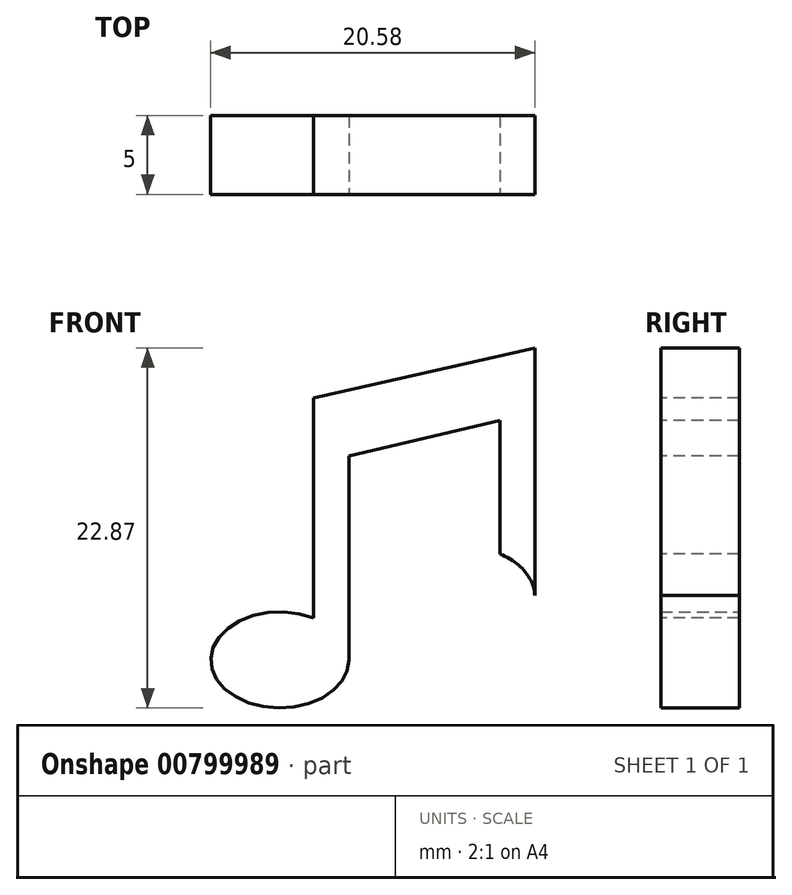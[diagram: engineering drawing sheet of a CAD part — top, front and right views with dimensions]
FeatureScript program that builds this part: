
annotation { "Feature Type Name" : "Feature", "Feature Type Description" : "" }
export const myFeature = defineFeature(function(context is Context, id is Id, definition is map)
    precondition{}
    {
        {
            var Q0;
            Q0=qCreatedBy(makeId("Front.planeOp"),FACE);
            var sketch = newSketch(context, id + "F0", { "sketchPlane" : qUnion([Q0])});
            skLineSegment(sketch, "E0", {"start": v(-6.22, 7.22) * mm, "end": v(7.82, 10.4) * mm});
            skLineSegment(sketch, "E1", {"start": v(7.82, 10.4) * mm, "end": v(7.82, -5.52) * mm});
            skLineSegment(sketch, "E2", {"start": v(-6.22, 7.22) * mm, "end": v(-6.22, -6.76) * mm});
            skLineSegment(sketch, "E3", {"start": v(-3.98, -9.42) * mm, "end": v(-3.98, 3.54) * mm});
            skLineSegment(sketch, "E4", {"start": v(-3.98, 3.54) * mm, "end": v(5.6, 5.78) * mm});
            skLineSegment(sketch, "E5", {"start": v(5.6, 5.78) * mm, "end": v(5.6, -2.69) * mm});
            skEllipse(sketch, "E6", {"center": v(-8.37, -9.42) * mm, "majorRadius": 4.39 * mm, "minorRadius": 3.05 * mm, "majorAxis": v(1, 0)});
            skEllipse(sketch, "E7", {"center": v(3.53, -5.32) * mm, "majorRadius": 4.3 * mm, "minorRadius": 3.06 * mm, "majorAxis": v(1, -0.05)});
            skSolve(sketch);
        }
        {
            var Q0;
            {var subQ3=sQuery(id+"F0.wireOp",EDGE,"E0");Q0=makeQuery(id+"F0.imprint","IMPRINT",FACE,{"disambiguationData":[TD([[makeQuery(id+"F0.imprint","IMPRINT",EDGE,{"derivedFrom":subQ3}),-1.0]])]});}
            var Q1;
            {var subQ0=sQuery(id+"F0.wireOp",EDGE,"E6");var subQ1=makeQuery(id+"F0.imprint","INTERSECT",VERTEX,{"derivedFrom":[sQuery(id+"F0.wireOp",EDGE,"E2"),subQ0]});Q1=makeQuery(id+"F0.imprint","IMPRINT",FACE,{"disambiguationData":[TD([[makeQuery(id+"F0.imprint","IMPRINT",EDGE,{"disambiguationData":[TD([[subQ1,1.0]])],"derivedFrom":subQ0}),1.0]])]});}
            var Q2;
            {var subQ0=sQuery(id+"F0.wireOp",EDGE,"E7");var subQ1=sQuery(id+"F0.wireOp",EDGE,"E1");var subQ2=makeQuery(id+"F0.imprint","INTERSECT",VERTEX,{"disambiguationData":[OD(0.0)],"derivedFrom":[subQ1,subQ0]});Q2=makeQuery(id+"F0.imprint","IMPRINT",FACE,{"disambiguationData":[TD([[makeQuery(id+"F0.imprint","IMPRINT",EDGE,{"disambiguationData":[TD([[subQ2,1.0]])],"derivedFrom":subQ1}),-1.0]])]});}
            extrude(context, id + "F1", {"entities" : qUnion([Q0, Q1, Q2]), "endBound" : BoundingType.SYMMETRIC, "oppositeDirection" : true, "depth" : 5 * mm, "offsetDistance" : 25 * mm});
        }
    });
